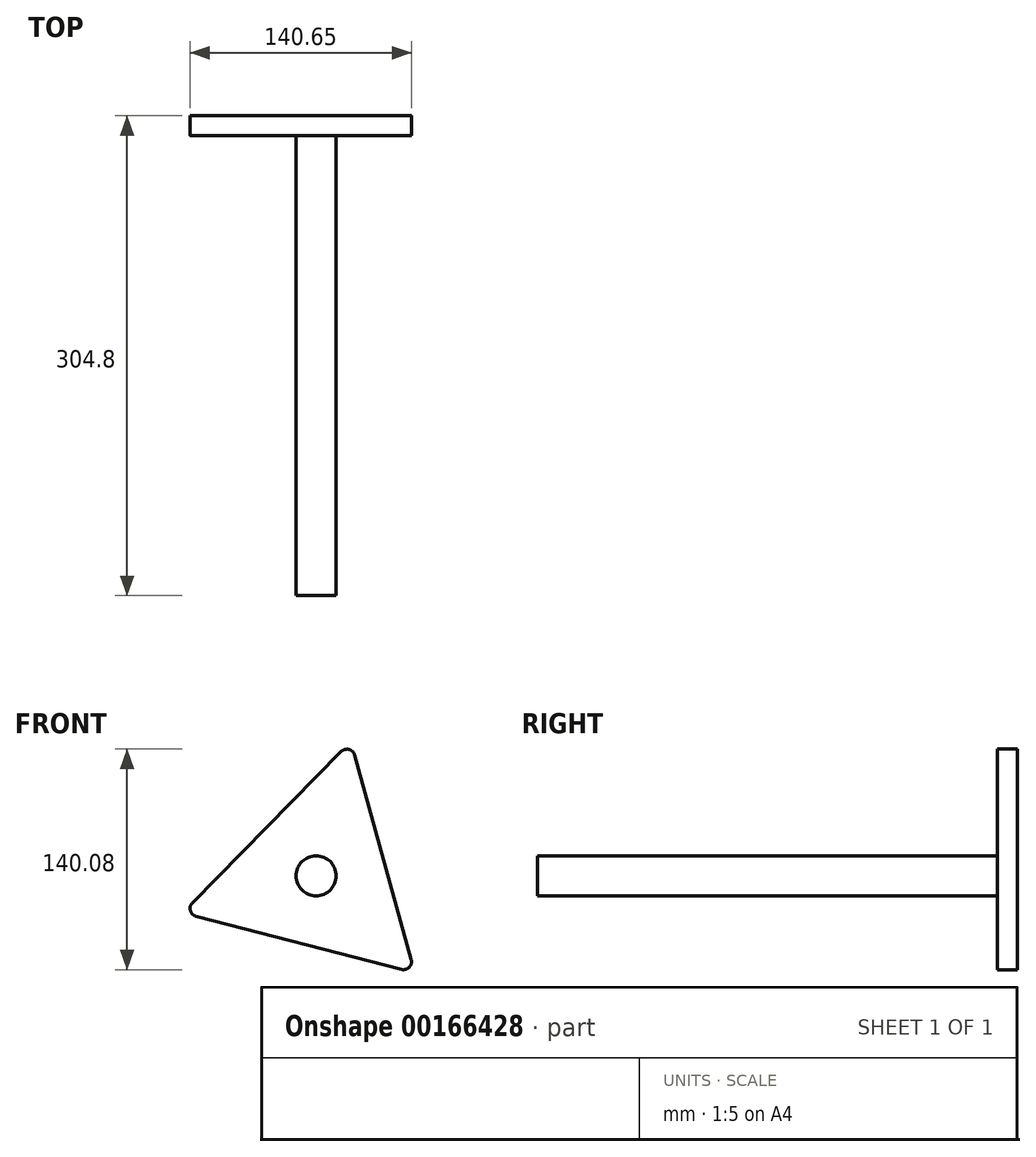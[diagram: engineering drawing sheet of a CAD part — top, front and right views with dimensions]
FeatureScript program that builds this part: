
annotation { "Feature Type Name" : "Feature", "Feature Type Description" : "" }
export const myFeature = defineFeature(function(context is Context, id is Id, definition is map)
    precondition{}
    {
        {
            var Q0;
            Q0=qCreatedBy(makeId("Front.planeOp"),FACE);
            var sketch = newSketch(context, id + "F0", { "sketchPlane" : qUnion([Q0])});
            skCircle(sketch, "E0.cCircle", {"center": v(0, 0) * mm, "radius": 44 * mm, "construction": true});
            skLineSegment(sketch, "E0.0", {"start": v(22.08, 85.17) * mm, "end": v(62.72, -61.7) * mm});
            skLineSegment(sketch, "E0.1", {"start": v(62.72, -61.7) * mm, "end": v(-84.8, -23.46) * mm});
            skLineSegment(sketch, "E0.2", {"start": v(-84.8, -23.46) * mm, "end": v(22.08, 85.17) * mm});
            skPoint(sketch, "E0.0.midPoint", {"position": v(42.4, 11.73) * mm});
            skCircle(sketch, "E1", {"center": v(0, 0) * mm, "radius": 12.7 * mm});
            skSolve(sketch);
        }
        {
            var Q0;
            Q0=makeQuery(id+"F0.imprint","IMPRINT",FACE,{"disambiguationData":[TD([[makeQuery(id+"F0.imprint","IMPRINT",EDGE,{"derivedFrom":sQuery(id+"F0.wireOp",EDGE,"E1")}),1.0]])]});
            extrude(context, id + "F1", {"entities" : qUnion([Q0]), "depth" : 304.8 * mm});
        }
        {
            var Q0;
            Q0 = qSketchRegion(id + "F0", true);
            extrude(context, id + "F2", {"entities" : qUnion([Q0]), "operationType" : NewBodyOperationType.ADD, "depth" : 12.7 * mm});
        }
        {
            var Q0;
            Q0=makeQuery(id+"F2.opExtrude","SWEPT_EDGE",EDGE,{"disambiguationData":[OSD([sQuery(id+"F0.wireOp",EDGE,"E0.1"),sQuery(id+"F0.wireOp",EDGE,"E0.2")])]});
            var Q1;
            Q1=makeQuery(id+"F2.opExtrude","SWEPT_EDGE",EDGE,{"disambiguationData":[OSD([sQuery(id+"F0.wireOp",EDGE,"E0.0"),sQuery(id+"F0.wireOp",EDGE,"E0.2")])]});
            var Q2;
            Q2=makeQuery(id+"F2.opExtrude","SWEPT_EDGE",EDGE,{"disambiguationData":[OSD([sQuery(id+"F0.wireOp",EDGE,"E0.0"),sQuery(id+"F0.wireOp",EDGE,"E0.1")])]});
            fillet(context, id + "F3", {"entities" : qUnion([Q0, Q1, Q2]), "radius" : 5.08 * mm, "tangentPropagation" : true, "allowEdgeOverflow" : false});
        }
    });
